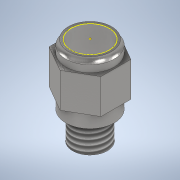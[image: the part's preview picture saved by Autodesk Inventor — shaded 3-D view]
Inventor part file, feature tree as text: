
AUTODESK INVENTOR PART (.ipt)
format: ipt  version: 2022 (Build 260153000, 153)  size: 169,984 bytes
history: native  units: mm
features: sketch x7, extrude x6, fillet x1, thread x1
ambient origin geometry x8: Origin, YZ Plane, XZ Plane, XY Plane, X Axis, Y Axis, Z Axis, Center Point
bodies: Solid1 (feature_tree)
feature tree (15):
  extrude  "Extrusion1"  Depth=7.0mm
  extrude  "Extrusion2"  Depth=14.0mm
  extrude  "Extrusion3"  Depth=10.0mm TaperAngle=0.0deg
  extrude  "Extrusion4"  Depth=2.0mm TaperAngle=0.0deg
  extrude  "Extrusion5"  Depth=8.0mm TaperAngle=0.0deg
  fillet  "Fillet1"  Radius=2.0mm
  thread  "Thread1"  [1 undecoded]
  extrude  "Extrusion6"  Depth=13.5mm TaperAngle=0.0deg
  sketch  "Sketch7"
  sketch  "Sketch1"  dims[d0=10.0mm d1=7.0mm]
  sketch  "Sketch2"  dims[d2=8.0mm d3=0.0mm d4=14.0mm]
  sketch  "Sketch3"  dims[d5=4.0mm d6=0.0mm d7=10.0mm d8=0.0mm]
  sketch  "Sketch4"  dims[d9=14.0mm d10=2.0mm d11=0.0mm]
  sketch  "Sketch5"  dims[d12=12.5mm d13=1.5mm d14=0.0mm d15=2.0mm d16=8.0mm d17=0.0mm]
  sketch  "Sketch6"  dims[d18=11.0mm d19=13.5mm d20=0.0mm]
note: 1 required parameter value undecoded (feature->parameter linkage not recoverable at this tier; creation-order binding heuristic only, values carry confidence <= 0.55)
